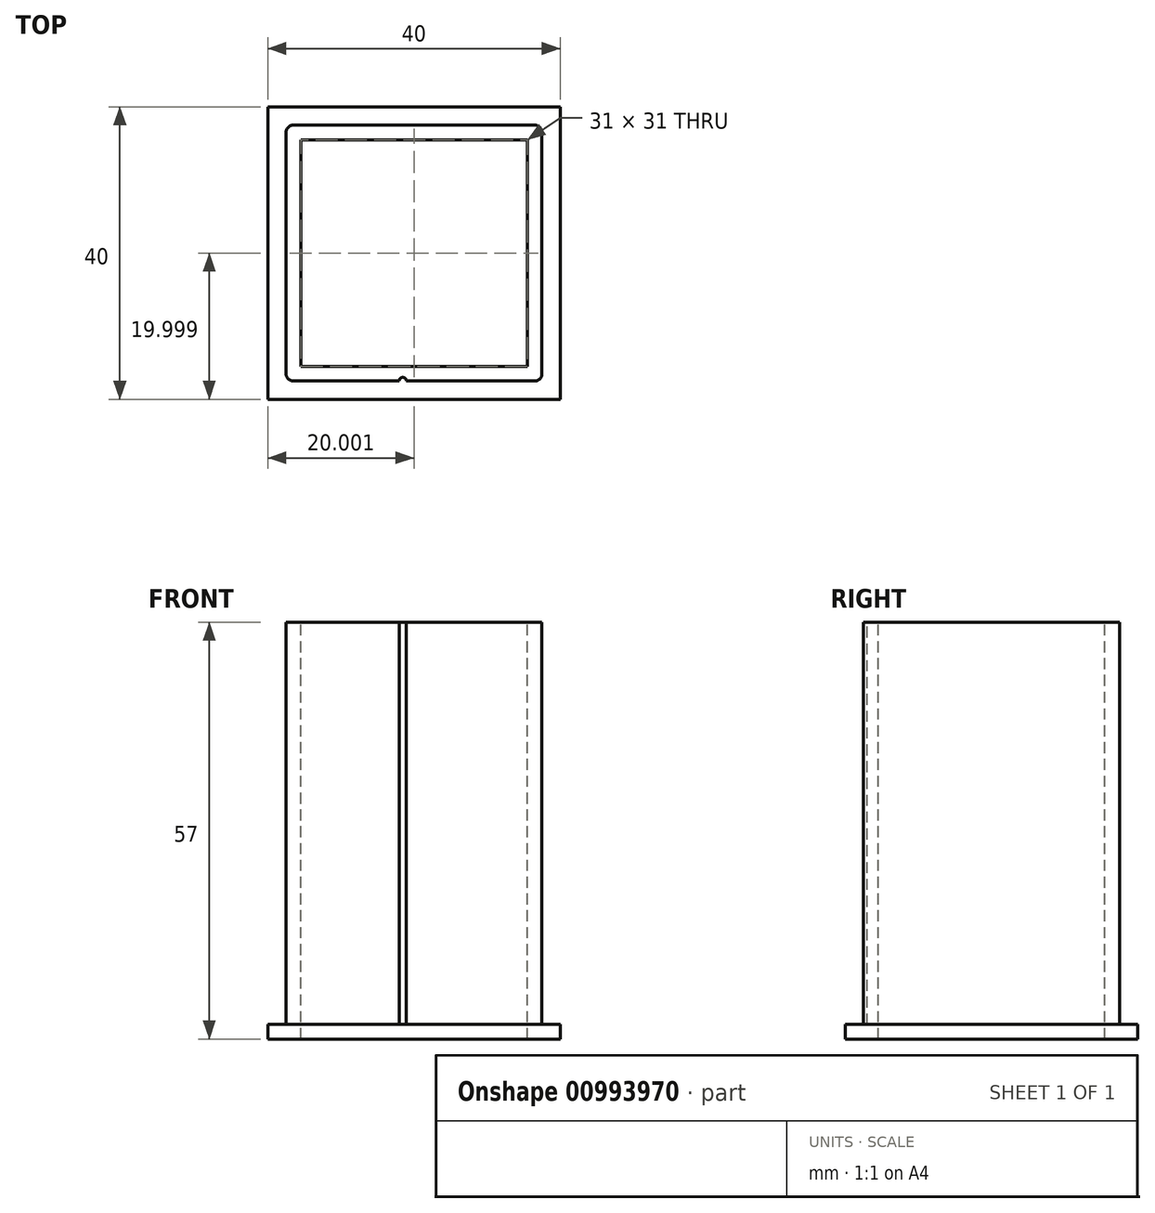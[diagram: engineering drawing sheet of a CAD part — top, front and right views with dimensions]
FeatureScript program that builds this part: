
annotation { "Feature Type Name" : "Feature", "Feature Type Description" : "" }
export const myFeature = defineFeature(function(context is Context, id is Id, definition is map)
    precondition{}
    {
        {
            var Q0;
            Q0=qCreatedBy(makeId("Top.planeOp"),FACE);
            var sketch = newSketch(context, id + "F0", { "sketchPlane" : qUnion([Q0])});
            skLineSegment(sketch, "E0.bottom", {"start": v(-23.98, 17.9) * mm, "end": v(16.02, 17.9) * mm});
            skLineSegment(sketch, "E0.top", {"start": v(-23.98, -22.1) * mm, "end": v(16.02, -22.1) * mm});
            skLineSegment(sketch, "E0.left", {"start": v(-23.98, 17.9) * mm, "end": v(-23.98, -22.1) * mm});
            skLineSegment(sketch, "E0.right", {"start": v(16.02, 17.9) * mm, "end": v(16.02, -22.1) * mm});
            skSolve(sketch);
        }
        {
            var Q0;
            Q0 = qSketchRegion(id + "F0", true);
            extrude(context, id + "F1", {"entities" : qUnion([Q0]), "depth" : 2 * mm, "offsetDistance" : 25 * mm});
        }
        {
            var Q0;
            Q0=makeQuery(id+"F1.opExtrude","CAP_FACE",FACE,{"disambiguationData":[OSD([sQuery(id+"F0.wireOp",EDGE,"E0.bottom"),sQuery(id+"F0.wireOp",EDGE,"E0.top"),sQuery(id+"F0.wireOp",EDGE,"E0.left"),sQuery(id+"F0.wireOp",EDGE,"E0.right")])],"isStart":false});
            var sketch = newSketch(context, id + "F2", { "sketchPlane" : qUnion([Q0])});
            skLineSegment(sketch, "E1.bottom", {"start": v(-21.48, 15.4) * mm, "end": v(13.52, 15.4) * mm});
            skLineSegment(sketch, "E1.top", {"start": v(-21.48, -19.6) * mm, "end": v(13.52, -19.6) * mm});
            skLineSegment(sketch, "E1.left", {"start": v(-21.48, 15.4) * mm, "end": v(-21.48, -19.6) * mm});
            skLineSegment(sketch, "E1.right", {"start": v(13.52, 15.4) * mm, "end": v(13.52, -19.6) * mm});
            skSolve(sketch);
        }
        {
            var Q0;
            Q0=makeQuery(id+"F2.imprint","IMPRINT",FACE,{"disambiguationData":[TD([[makeQuery(id+"F2.imprint","IMPRINT",EDGE,{"derivedFrom":sQuery(id+"F2.wireOp",EDGE,"E1.bottom")}),-1.0]])]});
            extrude(context, id + "F3", {"entities" : qUnion([Q0]), "operationType" : NewBodyOperationType.ADD, "depth" : 55 * mm, "offsetDistance" : 25 * mm});
        }
        {
            var Q0;
            Q0=makeQuery(id+"F3.opExtrude","CAP_FACE",FACE,{"disambiguationData":[OSD([sQuery(id+"F2.wireOp",EDGE,"E1.bottom"),sQuery(id+"F2.wireOp",EDGE,"E1.top"),sQuery(id+"F2.wireOp",EDGE,"E1.left"),sQuery(id+"F2.wireOp",EDGE,"E1.right")])],"isStart":false});
            var sketch = newSketch(context, id + "F4", { "sketchPlane" : qUnion([Q0])});
            skLineSegment(sketch, "E2.bottom", {"start": v(-19.48, -17.6) * mm, "end": v(11.52, -17.6) * mm});
            skLineSegment(sketch, "E2.top", {"start": v(-19.48, 13.4) * mm, "end": v(11.52, 13.4) * mm});
            skLineSegment(sketch, "E2.left", {"start": v(-19.48, -17.6) * mm, "end": v(-19.48, 13.4) * mm});
            skLineSegment(sketch, "E2.right", {"start": v(11.52, -17.6) * mm, "end": v(11.52, 13.4) * mm});
            skSolve(sketch);
        }
        {
            var Q0;
            Q0 = qSketchRegion(id + "F4", true);
            extrude(context, id + "F5", {"entities" : qUnion([Q0]), "operationType" : NewBodyOperationType.REMOVE, "endBound" : BoundingType.THROUGH_ALL, "oppositeDirection" : true, "depth" : 25 * mm, "offsetDistance" : 25 * mm});
        }
        {
            var Q0;
            Q0=makeQuery(id+"F3.opExtrude","SWEPT_EDGE",EDGE,{"disambiguationData":[OSD([sQuery(id+"F2.wireOp",EDGE,"E1.top"),sQuery(id+"F2.wireOp",EDGE,"E1.right")])]});
            var Q1;
            Q1=makeQuery(id+"F3.opExtrude","SWEPT_EDGE",EDGE,{"disambiguationData":[OSD([sQuery(id+"F2.wireOp",EDGE,"E1.bottom"),sQuery(id+"F2.wireOp",EDGE,"E1.right")])]});
            var Q2;
            Q2=makeQuery(id+"F3.opExtrude","SWEPT_EDGE",EDGE,{"disambiguationData":[OSD([sQuery(id+"F2.wireOp",EDGE,"E1.top"),sQuery(id+"F2.wireOp",EDGE,"E1.left")])]});
            var Q3;
            Q3=makeQuery(id+"F3.opExtrude","SWEPT_EDGE",EDGE,{"disambiguationData":[OSD([sQuery(id+"F2.wireOp",EDGE,"E1.bottom"),sQuery(id+"F2.wireOp",EDGE,"E1.left")])]});
            fillet(context, id + "F6", {"entities" : qUnion([Q0, Q1, Q2, Q3]), "radius" : 1 * mm, "tangentPropagation" : true, "allowEdgeOverflow" : false});
        }
        {
            var Q0;
            Q0=makeQuery(id+"F3.opExtrude","CAP_FACE",FACE,{"disambiguationData":[OSD([sQuery(id+"F2.wireOp",EDGE,"E1.bottom"),sQuery(id+"F2.wireOp",EDGE,"E1.top"),sQuery(id+"F2.wireOp",EDGE,"E1.left"),sQuery(id+"F2.wireOp",EDGE,"E1.right")])],"isStart":false});
            var sketch = newSketch(context, id + "F7", { "sketchPlane" : qUnion([Q0])});
            skCircle(sketch, "E3", {"center": v(-5.51, -19.6) * mm, "radius": 0.5 * mm});
            skSolve(sketch);
        }
        {
            var Q0;
            {var subQ0=sQuery(id+"F7.wireOp",EDGE,"E3");var subQ1=makeQuery(id+"F3.opExtrude","CAP_EDGE",EDGE,{"disambiguationData":[OSD([sQuery(id+"F2.wireOp",EDGE,"E1.top")])],"isStart":false});var subQ2=makeQuery(id+"F7.imprint","INTERSECT",VERTEX,{"disambiguationData":[OD(0.0)],"derivedFrom":[subQ1,subQ0]});Q0=makeQuery(id+"F7.imprint","IMPRINT",FACE,{"disambiguationData":[TD([[makeQuery(id+"F7.imprint","IMPRINT",EDGE,{"disambiguationData":[TD([[subQ2,1.0]])],"derivedFrom":subQ0}),1.0]])]});}
            var Q1;
            Q1=makeQuery(id+"F1.opExtrude","CAP_FACE",FACE,{"disambiguationData":[OSD([sQuery(id+"F0.wireOp",EDGE,"E0.bottom"),sQuery(id+"F0.wireOp",EDGE,"E0.top"),sQuery(id+"F0.wireOp",EDGE,"E0.left"),sQuery(id+"F0.wireOp",EDGE,"E0.right")])],"isStart":false});
            extrude(context, id + "F8", {"entities" : qUnion([Q0]), "operationType" : NewBodyOperationType.REMOVE, "endBound" : BoundingType.UP_TO_SURFACE, "oppositeDirection" : true, "depth" : 25 * mm, "endBoundEntityFace" : qUnion([Q1]), "offsetDistance" : 25 * mm});
        }
    });
